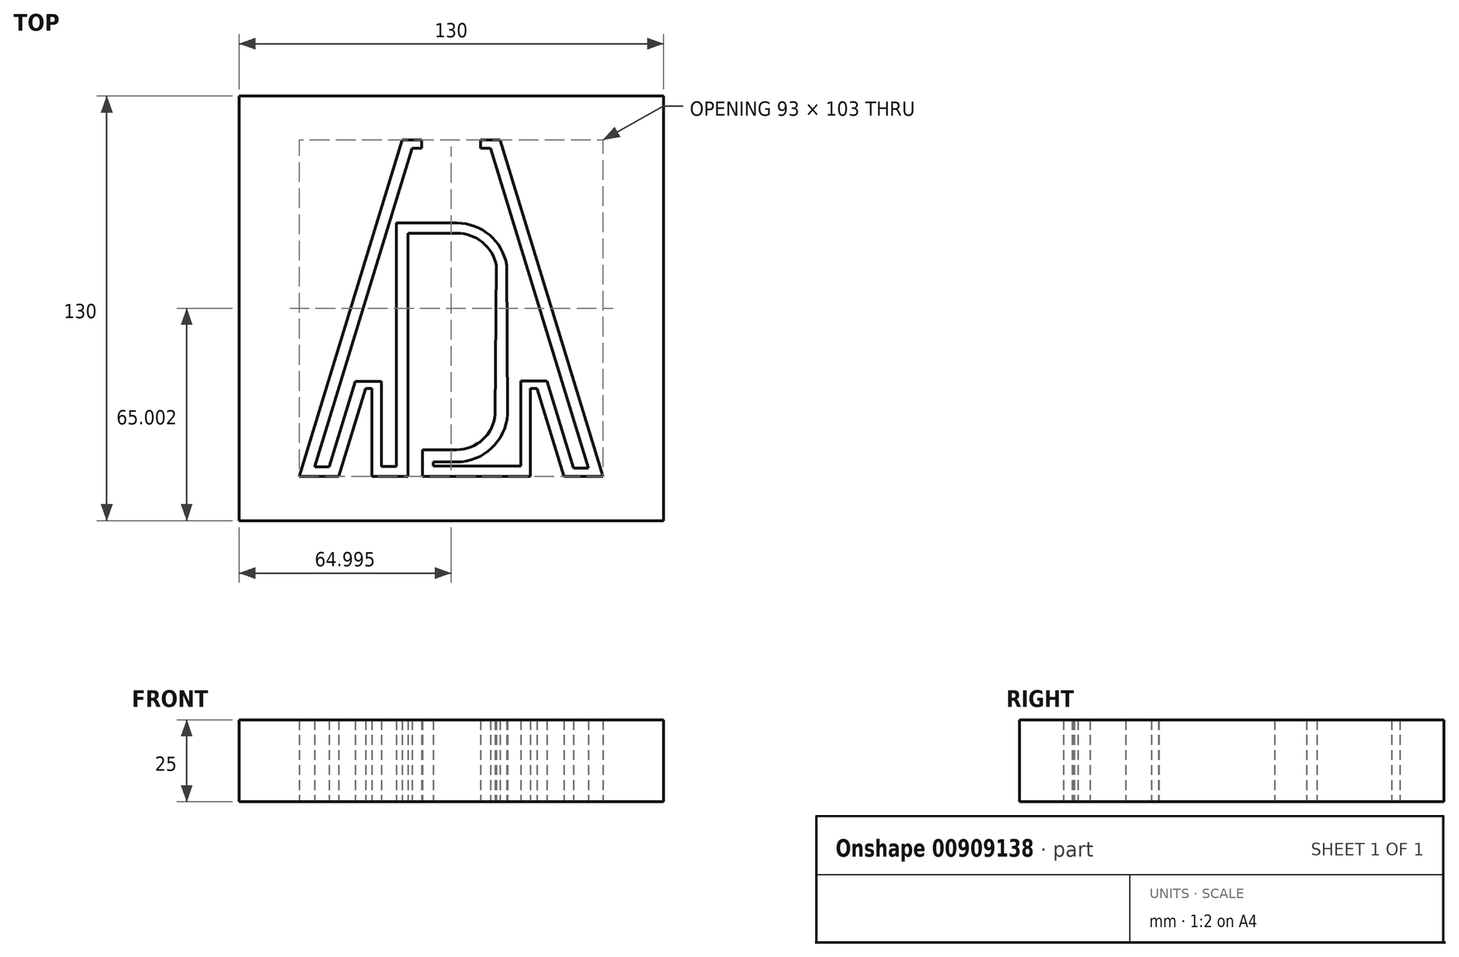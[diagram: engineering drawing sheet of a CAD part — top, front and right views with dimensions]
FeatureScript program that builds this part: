
annotation { "Feature Type Name" : "Feature", "Feature Type Description" : "" }
export const myFeature = defineFeature(function(context is Context, id is Id, definition is map)
    precondition{}
    {
        {
            var Q0;
            Q0=qCreatedBy(makeId("Top.planeOp"),FACE);
            var sketch = newSketch(context, id + "F0", { "sketchPlane" : qUnion([Q0])});
            skLineSegment(sketch, "E0", {"start": v(-9.6, 54.81) * mm, "end": v(-15.6, 54.81) * mm});
            skLineSegment(sketch, "E1", {"start": v(-15.6, 54.81) * mm, "end": v(-47.08, -48.19) * mm});
            skLineSegment(sketch, "E2", {"start": v(-47.08, -48.19) * mm, "end": v(-35.08, -48.19) * mm});
            skLineSegment(sketch, "E3", {"start": v(-35.08, -48.19) * mm, "end": v(-26.83, -21.19) * mm});
            skLineSegment(sketch, "E4", {"start": v(-26.83, -21.19) * mm, "end": v(-24.83, -21.19) * mm});
            skLineSegment(sketch, "E5", {"start": v(-24.83, -21.19) * mm, "end": v(-24.83, -48.19) * mm});
            skLineSegment(sketch, "E6", {"start": v(-24.83, -48.19) * mm, "end": v(-13.83, -48.19) * mm});
            skLineSegment(sketch, "E7", {"start": v(-13.83, -48.19) * mm, "end": v(-13.83, 26.31) * mm});
            skLineSegment(sketch, "E8", {"start": v(-13.83, 26.31) * mm, "end": v(1.17, 26.31) * mm});
            skLineSegment(sketch, "E9", {"start": v(1.05, -39.99) * mm, "end": v(-9.34, -39.99) * mm});
            skLineSegment(sketch, "E10", {"start": v(-9.34, -39.99) * mm, "end": v(-9.34, -48.19) * mm});
            skLineSegment(sketch, "E11", {"start": v(-9.34, -48.19) * mm, "end": v(23.66, -48.19) * mm});
            skLineSegment(sketch, "E12", {"start": v(23.66, -48.19) * mm, "end": v(23.66, -21.19) * mm});
            skLineSegment(sketch, "E13", {"start": v(23.66, -21.19) * mm, "end": v(25.66, -21.19) * mm});
            skLineSegment(sketch, "E14", {"start": v(25.66, -21.19) * mm, "end": v(33.92, -48.19) * mm});
            skLineSegment(sketch, "E15", {"start": v(33.92, -48.19) * mm, "end": v(45.92, -48.19) * mm});
            skLineSegment(sketch, "E16", {"start": v(45.92, -48.19) * mm, "end": v(14.43, 54.81) * mm});
            skLineSegment(sketch, "E17", {"start": v(14.43, 54.81) * mm, "end": v(8.43, 54.81) * mm});
            skLineSegment(sketch, "E18", {"start": v(-9.6, 54.81) * mm, "end": v(-9.6, 52.31) * mm});
            skLineSegment(sketch, "E19", {"start": v(-12.6, 52.31) * mm, "end": v(-42.41, -45.22) * mm});
            skLineSegment(sketch, "E20", {"start": v(-42.41, -45.22) * mm, "end": v(-37.91, -45.22) * mm});
            skLineSegment(sketch, "E21", {"start": v(-37.91, -45.22) * mm, "end": v(-29.93, -19.1) * mm});
            skLineSegment(sketch, "E22", {"start": v(-21.93, -45.1) * mm, "end": v(-17.43, -45.1) * mm});
            skLineSegment(sketch, "E23", {"start": v(-17.43, -45.1) * mm, "end": v(-17.43, 29.4) * mm});
            skLineSegment(sketch, "E24", {"start": v(-17.43, 29.4) * mm, "end": v(1.17, 29.4) * mm});
            skLineSegment(sketch, "E25", {"start": v(1.05, -43.7) * mm, "end": v(-6.1, -43.7) * mm});
            skLineSegment(sketch, "E26", {"start": v(-6.1, -43.7) * mm, "end": v(-6.1, -44.9) * mm});
            skLineSegment(sketch, "E27", {"start": v(-6.1, -44.9) * mm, "end": v(20.7, -44.9) * mm});
            skLineSegment(sketch, "E28", {"start": v(20.7, -44.9) * mm, "end": v(20.7, -18.9) * mm});
            skLineSegment(sketch, "E29", {"start": v(20.7, -18.9) * mm, "end": v(28.7, -18.9) * mm});
            skLineSegment(sketch, "E30", {"start": v(28.7, -18.9) * mm, "end": v(36.85, -45.56) * mm});
            skLineSegment(sketch, "E31", {"start": v(36.85, -45.56) * mm, "end": v(41.35, -45.56) * mm});
            skLineSegment(sketch, "E32", {"start": v(41.35, -45.56) * mm, "end": v(11.43, 52.31) * mm});
            skLineSegment(sketch, "E33", {"start": v(11.43, 52.31) * mm, "end": v(8.43, 52.31) * mm});
            skLineSegment(sketch, "E34", {"start": v(8.43, 54.81) * mm, "end": v(8.43, 52.31) * mm});
            skLineSegment(sketch, "E35", {"start": v(-12.6, 52.31) * mm, "end": v(-9.6, 52.31) * mm});
            skLineSegment(sketch, "E36", {"start": v(-29.93, -19.1) * mm, "end": v(-21.93, -19.1) * mm});
            skLineSegment(sketch, "E37", {"start": v(-21.93, -19.1) * mm, "end": v(-21.93, -45.1) * mm});
            skArc(sketch, "E38", {"start": v(1.05, -39.99) * mm, "mid": v(9.07, -36.85) * mm, "end": v(12.84, -29.1) * mm});
            skArc(sketch, "E39", {"start": v(13.22, 16.54) * mm, "mid": v(8.93, 23.56) * mm, "end": v(1.17, 26.31) * mm});
            skArc(sketch, "E40", {"start": v(16.4, 16.54) * mm, "mid": v(11.14, 25.76) * mm, "end": v(1.17, 29.4) * mm});
            skArc(sketch, "E41", {"start": v(1.05, -43.7) * mm, "mid": v(11.74, -39.49) * mm, "end": v(16.66, -29.1) * mm});
            skLineSegment(sketch, "E42", {"start": v(13.22, 16.54) * mm, "end": v(12.84, -29.1) * mm});
            skLineSegment(sketch, "E43", {"start": v(16.4, 16.54) * mm, "end": v(16.66, -29.1) * mm});
            skLineSegment(sketch, "E44.bottom", {"start": v(-65.58, 68.31) * mm, "end": v(64.42, 68.31) * mm});
            skLineSegment(sketch, "E44.top", {"start": v(-65.58, -61.69) * mm, "end": v(64.42, -61.69) * mm});
            skLineSegment(sketch, "E44.left", {"start": v(-65.58, 68.31) * mm, "end": v(-65.58, -61.69) * mm});
            skLineSegment(sketch, "E44.right", {"start": v(64.42, 68.31) * mm, "end": v(64.42, -61.69) * mm});
            skSolve(sketch);
        }
        {
            var Q0;
            Q0 = qSketchRegion(id + "F0", true);
            extrude(context, id + "F1", {"entities" : qUnion([Q0]), "depth" : 25 * mm, "offsetDistance" : 25 * mm});
        }
    });
